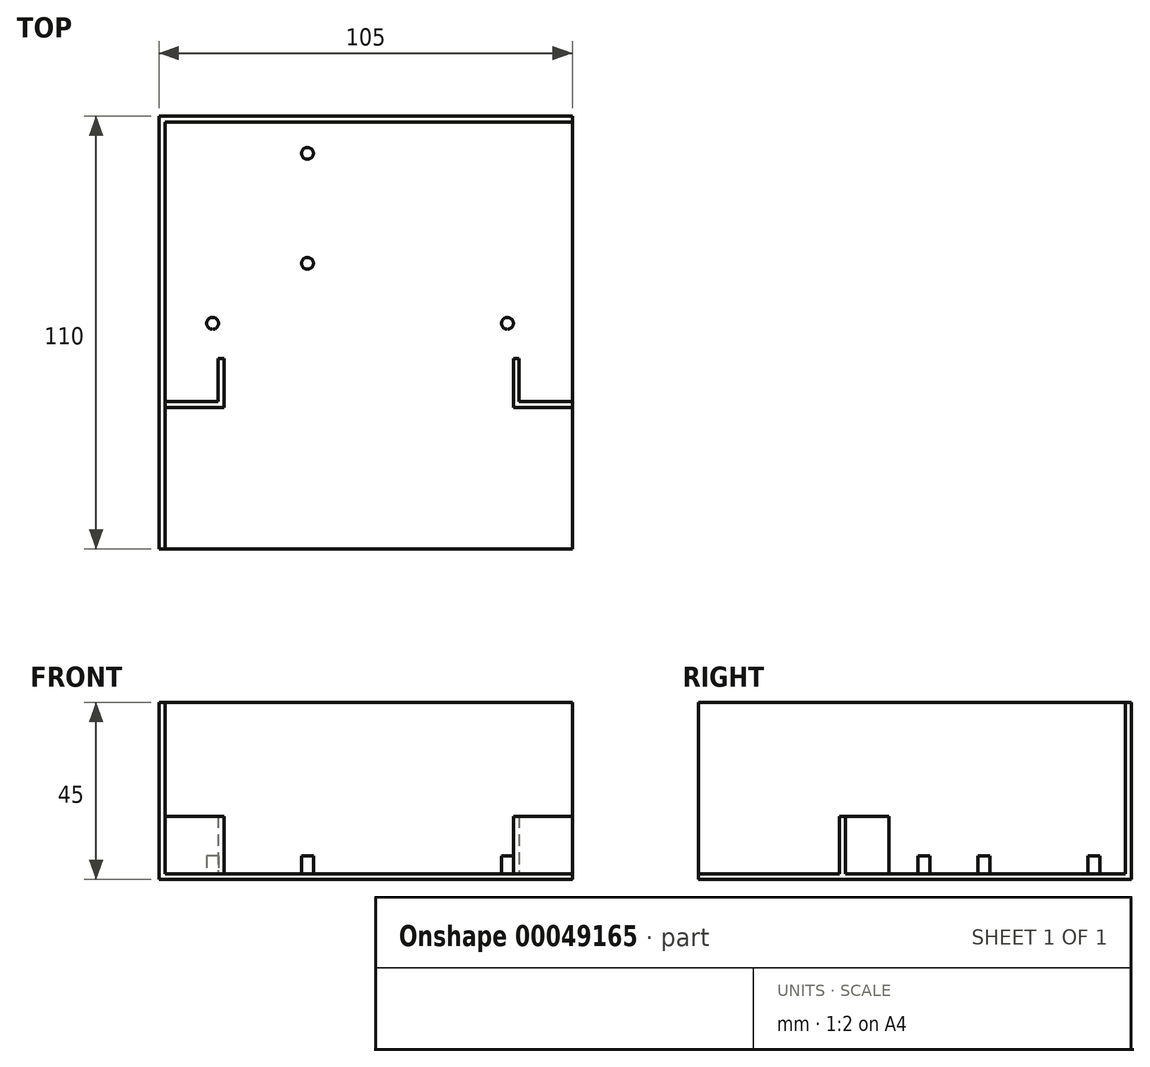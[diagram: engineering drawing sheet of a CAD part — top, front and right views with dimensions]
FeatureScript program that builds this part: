
annotation { "Feature Type Name" : "Feature", "Feature Type Description" : "" }
export const myFeature = defineFeature(function(context is Context, id is Id, definition is map)
    precondition{}
    {
        {
            var Q0;
            Q0=qCreatedBy(makeId("Top.planeOp"),FACE);
            var sketch = newSketch(context, id + "F0", { "sketchPlane" : qUnion([Q0])});
            skLineSegment(sketch, "E0.rect.bottom", {"start": v(52.5, 55) * mm, "end": v(-52.5, 55) * mm});
            skLineSegment(sketch, "E0.rect.top", {"start": v(52.5, -55) * mm, "end": v(-52.5, -55) * mm});
            skLineSegment(sketch, "E0.rect.left", {"start": v(52.5, 55) * mm, "end": v(52.5, -55) * mm});
            skLineSegment(sketch, "E0.rect.right", {"start": v(-52.5, 55) * mm, "end": v(-52.5, -55) * mm});
            skPoint(sketch, "E0.rect.middle", {"position": v(0, 0) * mm});
            skSolve(sketch);
        }
        {
            var Q0;
            Q0=makeQuery(id+"F0.imprint","IMPRINT",FACE,{"disambiguationData":[TD([[makeQuery(id+"F0.imprint","IMPRINT",EDGE,{"derivedFrom":sQuery(id+"F0.wireOp",EDGE,"E0.rect.bottom")}),1.0]])]});
            extrude(context, id + "F1", {"entities" : qUnion([Q0]), "depth" : 1.5 * mm});
        }
        {
            var Q0;
            Q0=makeQuery(id+"F1.opExtrude","CAP_FACE",FACE,{"disambiguationData":[OSD([sQuery(id+"F0.wireOp",EDGE,"E0.rect.bottom"),sQuery(id+"F0.wireOp",EDGE,"E0.rect.top"),sQuery(id+"F0.wireOp",EDGE,"E0.rect.left"),sQuery(id+"F0.wireOp",EDGE,"E0.rect.right")])],"isStart":false});
            var sketch = newSketch(context, id + "F2", { "sketchPlane" : qUnion([Q0])});
            skLineSegment(sketch, "E1.bottom", {"start": v(-52.5, 55) * mm, "end": v(52.5, 55) * mm});
            skLineSegment(sketch, "E1.top", {"start": v(-52.5, 53.5) * mm, "end": v(52.5, 53.5) * mm});
            skLineSegment(sketch, "E1.left", {"start": v(-52.5, 55) * mm, "end": v(-52.5, 53.5) * mm});
            skLineSegment(sketch, "E1.right", {"start": v(52.5, 55) * mm, "end": v(52.5, 53.5) * mm});
            skSolve(sketch);
        }
        {
            var Q0;
            Q0=makeQuery(id+"F2.imprint","IMPRINT",FACE,{"disambiguationData":[TD([[makeQuery(id+"F2.imprint","IMPRINT",EDGE,{"derivedFrom":sQuery(id+"F2.wireOp",EDGE,"E1.bottom")}),1.0]])]});
            extrude(context, id + "F3", {"entities" : qUnion([Q0]), "operationType" : NewBodyOperationType.ADD, "depth" : 43.5 * mm});
        }
        {
            var Q0;
            Q0=makeQuery(id+"F1.opExtrude","CAP_FACE",FACE,{"disambiguationData":[OSD([sQuery(id+"F0.wireOp",EDGE,"E0.rect.bottom"),sQuery(id+"F0.wireOp",EDGE,"E0.rect.top"),sQuery(id+"F0.wireOp",EDGE,"E0.rect.left"),sQuery(id+"F0.wireOp",EDGE,"E0.rect.right")])],"isStart":false});
            var sketch = newSketch(context, id + "F4", { "sketchPlane" : qUnion([Q0])});
            skLineSegment(sketch, "E2.bottom", {"start": v(-52.5, -55) * mm, "end": v(-51, -55) * mm});
            skLineSegment(sketch, "E2.top", {"start": v(-52.5, 53.5) * mm, "end": v(-51, 53.5) * mm});
            skLineSegment(sketch, "E2.left", {"start": v(-52.5, -55) * mm, "end": v(-52.5, 53.5) * mm});
            skLineSegment(sketch, "E2.right", {"start": v(-51, -55) * mm, "end": v(-51, 53.5) * mm});
            skSolve(sketch);
        }
        {
            var Q0;
            Q0=makeQuery(id+"F4.imprint","IMPRINT",FACE,{"disambiguationData":[TD([[makeQuery(id+"F4.imprint","IMPRINT",EDGE,{"derivedFrom":sQuery(id+"F4.wireOp",EDGE,"E2.bottom")}),-1.0]])]});
            extrude(context, id + "F5", {"entities" : qUnion([Q0]), "operationType" : NewBodyOperationType.ADD, "depth" : 43.5 * mm});
        }
        {
            var Q0;
            Q0=makeQuery(id+"F1.opExtrude","CAP_FACE",FACE,{"disambiguationData":[OSD([sQuery(id+"F0.wireOp",EDGE,"E0.rect.bottom"),sQuery(id+"F0.wireOp",EDGE,"E0.rect.top"),sQuery(id+"F0.wireOp",EDGE,"E0.rect.left"),sQuery(id+"F0.wireOp",EDGE,"E0.rect.right")])],"isStart":false});
            var sketch = newSketch(context, id + "F6", { "sketchPlane" : qUnion([Q0])});
            skCircle(sketch, "E3", {"center": v(-14.8, 45.5) * mm, "radius": 1.5 * mm});
            skCircle(sketch, "E4", {"center": v(-14.8, 17.56) * mm, "radius": 1.5 * mm});
            skCircle(sketch, "E5", {"center": v(-38.9, 2.3) * mm, "radius": 1.5 * mm});
            skCircle(sketch, "E6", {"center": v(36, 2.3) * mm, "radius": 1.5 * mm});
            skSolve(sketch);
        }
        {
            var Q0;
            Q0=qSketchRegion(id+"F6",true);
            extrude(context, id + "F7", {"entities" : qUnion([Q0]), "operationType" : NewBodyOperationType.ADD, "depth" : 4.5 * mm});
        }
        {
            var Q0;
            Q0=makeQuery(id+"F1.opExtrude","CAP_FACE",FACE,{"disambiguationData":[OSD([sQuery(id+"F0.wireOp",EDGE,"E0.rect.bottom"),sQuery(id+"F0.wireOp",EDGE,"E0.rect.top"),sQuery(id+"F0.wireOp",EDGE,"E0.rect.left"),sQuery(id+"F0.wireOp",EDGE,"E0.rect.right")])],"isStart":false});
            var sketch = newSketch(context, id + "F8", { "sketchPlane" : qUnion([Q0])});
            skLineSegment(sketch, "E7.bottom", {"start": v(-51, -17.6) * mm, "end": v(-36, -17.6) * mm});
            skLineSegment(sketch, "E7.top", {"start": v(-51, -19.1) * mm, "end": v(-36, -19.1) * mm});
            skLineSegment(sketch, "E7.left", {"start": v(-51, -17.6) * mm, "end": v(-51, -19.1) * mm});
            skLineSegment(sketch, "E7.right", {"start": v(-36, -17.6) * mm, "end": v(-36, -19.1) * mm});
            skLineSegment(sketch, "E8.bottom", {"start": v(-36, -17.6) * mm, "end": v(-37.5, -17.6) * mm});
            skLineSegment(sketch, "E8.top", {"start": v(-36, -6.6) * mm, "end": v(-37.5, -6.6) * mm});
            skLineSegment(sketch, "E8.left", {"start": v(-36, -17.6) * mm, "end": v(-36, -6.6) * mm});
            skLineSegment(sketch, "E8.right", {"start": v(-37.5, -17.6) * mm, "end": v(-37.5, -6.6) * mm});
            skLineSegment(sketch, "E9.bottom", {"start": v(52.5, -19.1) * mm, "end": v(37.5, -19.1) * mm});
            skLineSegment(sketch, "E9.top", {"start": v(52.5, -17.6) * mm, "end": v(37.5, -17.6) * mm});
            skLineSegment(sketch, "E9.left", {"start": v(52.5, -19.1) * mm, "end": v(52.5, -17.6) * mm});
            skLineSegment(sketch, "E9.right", {"start": v(37.5, -19.1) * mm, "end": v(37.5, -17.6) * mm});
            skLineSegment(sketch, "E10.bottom", {"start": v(37.5, -17.6) * mm, "end": v(39, -17.6) * mm});
            skLineSegment(sketch, "E10.top", {"start": v(37.5, -6.6) * mm, "end": v(39, -6.6) * mm});
            skLineSegment(sketch, "E10.left", {"start": v(37.5, -17.6) * mm, "end": v(37.5, -6.6) * mm});
            skLineSegment(sketch, "E10.right", {"start": v(39, -17.6) * mm, "end": v(39, -6.6) * mm});
            skSolve(sketch);
        }
        {
            var Q0;
            Q0=qSketchRegion(id+"F8",true);
            extrude(context, id + "F9", {"entities" : qUnion([Q0]), "operationType" : NewBodyOperationType.ADD, "depth" : 14.6 * mm});
        }
    });
